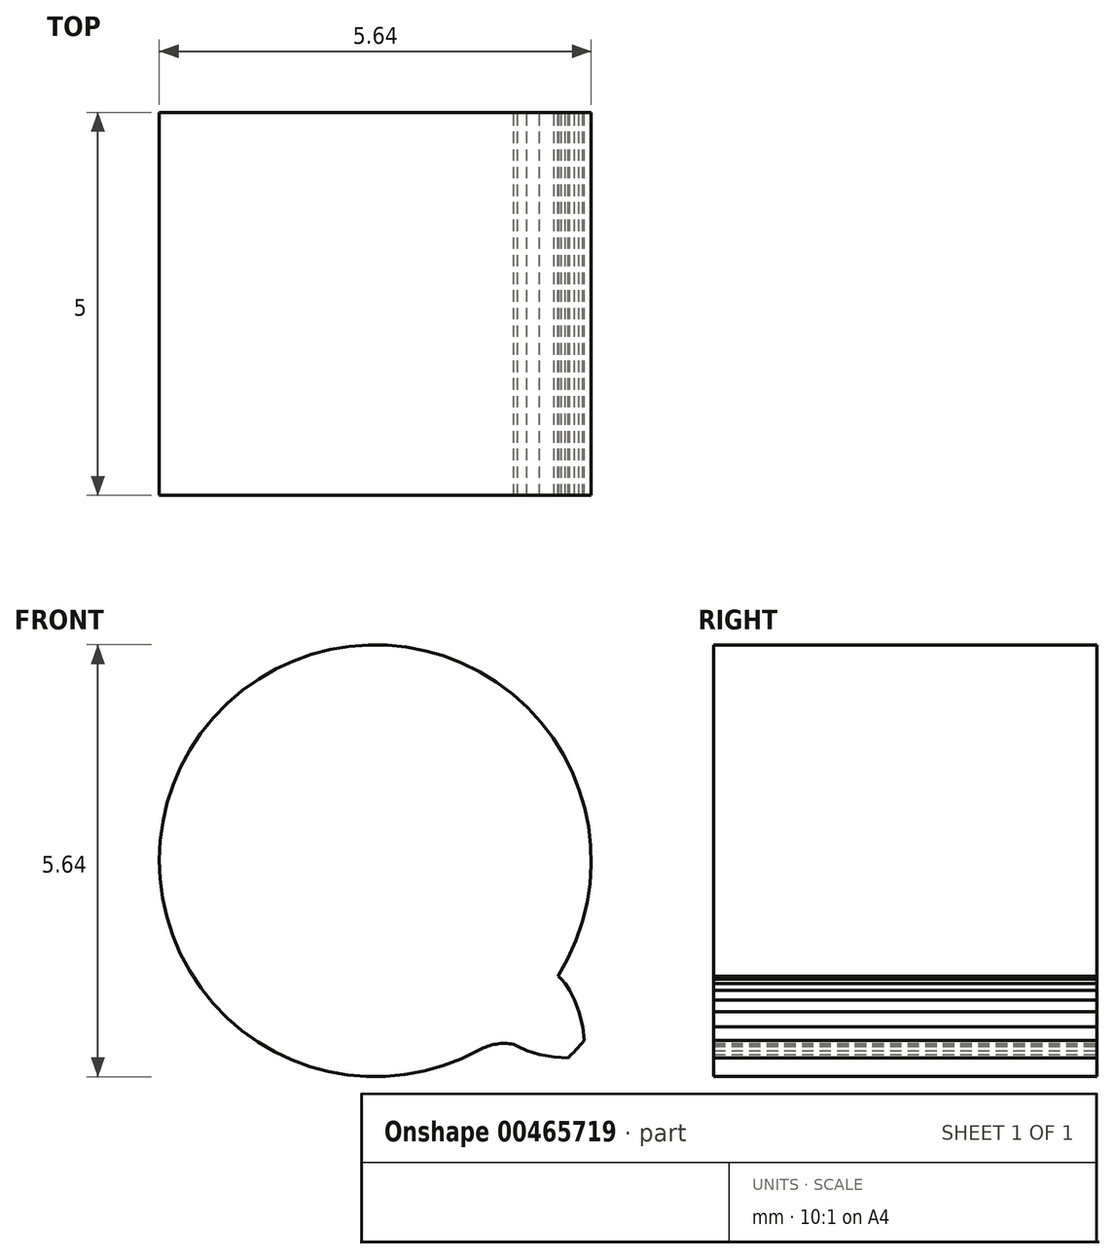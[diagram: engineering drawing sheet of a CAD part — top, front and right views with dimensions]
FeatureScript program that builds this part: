
annotation { "Feature Type Name" : "Feature", "Feature Type Description" : "" }
export const myFeature = defineFeature(function(context is Context, id is Id, definition is map)
    precondition{}
    {
        {
            var Q0;
            Q0=qCreatedBy(makeId("Front.planeOp"),FACE);
            var sketch = newSketch(context, id + "F0", { "sketchPlane" : qUnion([Q0])});
            skCircle(sketch, "E0", {"center": v(0, 0) * mm, "radius": 2.82 * mm});
            skCircle(sketch, "E1", {"center": v(0, 0) * mm, "radius": 3 * mm, "construction": true});
            skCircle(sketch, "E2", {"center": v(0, 0) * mm, "radius": 3.6 * mm, "construction": true});
            skLineSegment(sketch, "E3", {"start": v(0, 0) * mm, "end": v(0, 4.6) * mm, "construction": true});
            skLineSegment(sketch, "E4", {"start": v(0, 4.6) * mm, "end": v(0, 0) * mm, "construction": true});
            skLineSegment(sketch, "E5", {"start": v(0, 0) * mm, "end": v(-1.55, 4.33) * mm, "construction": true});
            skLineSegment(sketch, "E6", {"start": v(0, 2.82) * mm, "end": v(-2.7, 2.82) * mm, "construction": true});
            skLineSegment(sketch, "E7", {"start": v(0, 0) * mm, "end": v(-2.58, 3.55) * mm, "construction": true});
            skLineSegment(sketch, "E8", {"start": v(0, 0) * mm, "end": v(-1.24, 3.81) * mm, "construction": true});
            skLineSegment(sketch, "E9", {"start": v(0, 2.82) * mm, "end": v(2.06, 2.82) * mm, "construction": true});
            skLineSegment(sketch, "E10", {"start": v(0, 0) * mm, "end": v(-0.4, 3.74) * mm, "construction": true});
            skLineSegment(sketch, "E11", {"start": v(0, 0) * mm, "end": v(-0.82, 3.85) * mm, "construction": true});
            skLineSegment(sketch, "E12", {"start": v(0, 0) * mm, "end": v(-1.63, 3.66) * mm, "construction": true});
            skLineSegment(sketch, "E13", {"start": v(-0.3, 2.8) * mm, "end": v(0, 2.83) * mm, "construction": true});
            skLineSegment(sketch, "E14", {"start": v(-0.59, 2.76) * mm, "end": v(0, 2.88) * mm, "construction": true});
            skLineSegment(sketch, "E15", {"start": v(-0.87, 2.68) * mm, "end": v(-0.03, 2.95) * mm, "construction": true});
            skLineSegment(sketch, "E16", {"start": v(-1.15, 2.58) * mm, "end": v(-0.08, 3.05) * mm, "construction": true});
            skLineSegment(sketch, "E17", {"start": v(0, 0) * mm, "end": v(-1.97, 3.41) * mm, "construction": true});
            skLineSegment(sketch, "E18", {"start": v(-1.4, 2.44) * mm, "end": v(-0.15, 3.17) * mm, "construction": true});
            skLineSegment(sketch, "E19", {"start": v(-1.66, 2.28) * mm, "end": v(-0.25, 3.3) * mm, "construction": true});
            skLineSegment(sketch, "E20", {"start": v(0, 0) * mm, "end": v(-2.7, 3) * mm, "construction": true});
            skLineSegment(sketch, "E21", {"start": v(-1.89, 2.1) * mm, "end": v(-0.38, 3.45) * mm, "construction": true});
            skLineSegment(sketch, "E22", {"start": v(0, 2.82) * mm, "end": v(0, 2.83) * mm});
            skLineSegment(sketch, "E23", {"start": v(0, 2.88) * mm, "end": v(0, 2.83) * mm});
            skLineSegment(sketch, "E24", {"start": v(0, 2.88) * mm, "end": v(-0.03, 2.95) * mm});
            skLineSegment(sketch, "E25", {"start": v(-0.03, 2.95) * mm, "end": v(-0.08, 3.05) * mm});
            skLineSegment(sketch, "E26", {"start": v(-0.08, 3.05) * mm, "end": v(-0.15, 3.17) * mm});
            skLineSegment(sketch, "E27", {"start": v(-0.15, 3.17) * mm, "end": v(-0.25, 3.3) * mm});
            skLineSegment(sketch, "E28", {"start": v(-0.25, 3.3) * mm, "end": v(-0.38, 3.45) * mm});
            skLineSegment(sketch, "E29", {"start": v(0, 0) * mm, "end": v(-2.88, 2.6) * mm, "construction": true});
            skLineSegment(sketch, "E30", {"start": v(-2.1, 1.89) * mm, "end": v(-0.56, 3.6) * mm, "construction": true});
            skLineSegment(sketch, "E31", {"start": v(-0.56, 3.6) * mm, "end": v(-0.38, 3.45) * mm});
            skLineSegment(sketch, "E32", {"start": v(0, 0) * mm, "end": v(-0.81, 4.25) * mm});
            skLineSegment(sketch, "E33.MirrorCS", {"start": v(-0.8, 3.54) * mm, "end": v(-0.92, 3.34) * mm});
            skLineSegment(sketch, "E34.MirrorCS", {"start": v(-1, 3.16) * mm, "end": v(-0.92, 3.34) * mm});
            skLineSegment(sketch, "E35.MirrorCS", {"start": v(-1.04, 3) * mm, "end": v(-1, 3.16) * mm});
            skLineSegment(sketch, "E36.MirrorCS", {"start": v(-1.06, 2.86) * mm, "end": v(-1.04, 3) * mm});
            skLineSegment(sketch, "E37.MirrorCS", {"start": v(-1.06, 2.76) * mm, "end": v(-1.06, 2.86) * mm});
            skLineSegment(sketch, "E38.MirrorCS", {"start": v(-1.06, 2.68) * mm, "end": v(-1.06, 2.76) * mm});
            skLineSegment(sketch, "E39.MirrorCS", {"start": v(-1.06, 2.68) * mm, "end": v(-1.05, 2.63) * mm});
            skLineSegment(sketch, "E40.MirrorCS", {"start": v(-1.04, 2.62) * mm, "end": v(-1.05, 2.63) * mm});
            skArc(sketch, "E41", {"start": v(-0.52, 3.56) * mm, "mid": v(-0.68, 3.54) * mm, "end": v(-0.83, 3.5) * mm});
            skLineSegment(sketch, "E42", {"start": v(-0.05, 3) * mm, "end": v(0, 0) * mm, "construction": true});
            skLineSegment(sketch, "E43", {"start": v(0, 0) * mm, "end": v(-2.64, 3.5) * mm, "construction": true});
            skArc(sketch, "E44", {"start": v(-1.8, 2.4) * mm, "mid": v(-1.36, 2.47) * mm, "end": v(-1.06, 2.8) * mm});
            skLineSegment(sketch, "E45", {"start": v(0, 0) * mm, "end": v(-1.74, 5.05) * mm, "construction": true});
            skSolve(sketch);
        }
        {
            var Q0;
            Q0=qCreatedBy(makeId("Front.planeOp"),FACE);
            var sketch = newSketch(context, id + "F1", { "sketchPlane" : qUnion([Q0])});
            skCircle(sketch, "E46.0", {"center": v(0, 0) * mm, "radius": 2.82 * mm});
            skArc(sketch, "E47.0", {"start": v(-0.52, 3.56) * mm, "mid": v(-0.68, 3.54) * mm, "end": v(-0.83, 3.5) * mm});
            skLineSegment(sketch, "E47.1", {"start": v(-0.8, 3.54) * mm, "end": v(-0.92, 3.34) * mm});
            skLineSegment(sketch, "E47.2", {"start": v(-1, 3.16) * mm, "end": v(-0.92, 3.34) * mm});
            skLineSegment(sketch, "E47.3", {"start": v(-1.04, 3) * mm, "end": v(-1, 3.16) * mm});
            skLineSegment(sketch, "E47.4", {"start": v(-0.56, 3.6) * mm, "end": v(-0.38, 3.45) * mm});
            skLineSegment(sketch, "E47.5", {"start": v(-0.25, 3.3) * mm, "end": v(-0.38, 3.45) * mm});
            skLineSegment(sketch, "E47.6", {"start": v(-0.15, 3.17) * mm, "end": v(-0.25, 3.3) * mm});
            skLineSegment(sketch, "E47.7", {"start": v(-0.08, 3.05) * mm, "end": v(-0.15, 3.17) * mm});
            skLineSegment(sketch, "E47.8", {"start": v(-0.03, 2.95) * mm, "end": v(-0.08, 3.05) * mm});
            skLineSegment(sketch, "E47.9", {"start": v(0, 2.88) * mm, "end": v(-0.03, 2.95) * mm});
            skLineSegment(sketch, "E47.10", {"start": v(0, 2.88) * mm, "end": v(0, 2.83) * mm});
            skLineSegment(sketch, "E47.11", {"start": v(0, 2.82) * mm, "end": v(0, 2.83) * mm});
            skLineSegment(sketch, "E47.12", {"start": v(-1.06, 2.86) * mm, "end": v(-1.04, 3) * mm});
            skLineSegment(sketch, "E47.13", {"start": v(-1.06, 2.76) * mm, "end": v(-1.06, 2.86) * mm});
            skLineSegment(sketch, "E47.14", {"start": v(-1.06, 2.68) * mm, "end": v(-1.06, 2.76) * mm});
            skLineSegment(sketch, "E47.15", {"start": v(-1.06, 2.68) * mm, "end": v(-1.05, 2.63) * mm});
            skLineSegment(sketch, "E47.16", {"start": v(-1.04, 2.62) * mm, "end": v(-1.05, 2.63) * mm});
            skArc(sketch, "E48.0", {"start": v(-1.8, 2.4) * mm, "mid": v(-1.36, 2.47) * mm, "end": v(-1.06, 2.8) * mm});
            skArc(sketch, "E49.MirrorCS", {"start": v(0.8, 2.9) * mm, "mid": v(0.35, 2.8) * mm, "end": v(-0.05, 3) * mm});
            skArc(sketch, "E50.MirrorCS", {"start": v(-0.83, 3.5) * mm, "mid": v(-0.68, 3.54) * mm, "end": v(-0.52, 3.56) * mm});
            skLineSegment(sketch, "E51", {"start": v(-1.69, 3.06) * mm, "end": v(0, 0) * mm, "construction": true});
            skLineSegment(sketch, "E52.MirrorCS", {"start": v(-2.38, 1.5) * mm, "end": v(-2.4, 1.52) * mm});
            skLineSegment(sketch, "E53.MirrorCS", {"start": v(-2.43, 1.55) * mm, "end": v(-2.4, 1.52) * mm});
            skLineSegment(sketch, "E54.MirrorCS", {"start": v(-2.43, 1.55) * mm, "end": v(-2.48, 1.6) * mm});
            skLineSegment(sketch, "E55.MirrorCS", {"start": v(-2.48, 1.6) * mm, "end": v(-2.54, 1.7) * mm});
            skLineSegment(sketch, "E56.MirrorCS", {"start": v(-1.7, 2.32) * mm, "end": v(-1.67, 2.3) * mm});
            skLineSegment(sketch, "E57.MirrorCS", {"start": v(-1.7, 2.32) * mm, "end": v(-1.76, 2.37) * mm});
            skLineSegment(sketch, "E58.MirrorCS", {"start": v(-1.66, 2.28) * mm, "end": v(-1.67, 2.3) * mm});
            skLineSegment(sketch, "E59.MirrorCS", {"start": v(-1.76, 2.37) * mm, "end": v(-1.86, 2.42) * mm});
            skLineSegment(sketch, "E60.MirrorCS", {"start": v(-1.98, 2.48) * mm, "end": v(-2.14, 2.53) * mm});
            skLineSegment(sketch, "E61.MirrorCS", {"start": v(-1.86, 2.42) * mm, "end": v(-1.98, 2.48) * mm});
            skLineSegment(sketch, "E62.MirrorCS", {"start": v(-2.54, 1.7) * mm, "end": v(-2.6, 1.82) * mm});
            skLineSegment(sketch, "E63.MirrorCS", {"start": v(-2.6, 1.82) * mm, "end": v(-2.66, 1.97) * mm});
            skLineSegment(sketch, "E64.MirrorCS", {"start": v(-2.66, 1.97) * mm, "end": v(-2.7, 2.17) * mm});
            skLineSegment(sketch, "E65.MirrorCS", {"start": v(-2.56, 2.58) * mm, "end": v(-2.34, 2.56) * mm});
            skLineSegment(sketch, "E66.MirrorCS", {"start": v(-2.74, 2.4) * mm, "end": v(-2.7, 2.17) * mm});
            skArc(sketch, "E67.MirrorCS", {"start": v(-2.52, 2.57) * mm, "mid": v(-2.63, 2.46) * mm, "end": v(-2.73, 2.35) * mm});
            skLineSegment(sketch, "E68.MirrorCS", {"start": v(-2.14, 2.53) * mm, "end": v(-2.34, 2.56) * mm});
            skArc(sketch, "E69.MirrorCS", {"start": v(-1.06, 2.8) * mm, "mid": v(-1.36, 2.47) * mm, "end": v(-1.8, 2.4) * mm});
            skArc(sketch, "E70.MirrorCS", {"start": v(-2.73, 2.35) * mm, "mid": v(-2.63, 2.46) * mm, "end": v(-2.52, 2.57) * mm});
            skArc(sketch, "E71.MirrorCS", {"start": v(-2.87, 0.88) * mm, "mid": v(-2.55, 1.2) * mm, "end": v(-2.5, 1.65) * mm});
            skLineSegment(sketch, "E72", {"start": v(-3.16, 1.48) * mm, "end": v(0, 0) * mm, "construction": true});
            skLineSegment(sketch, "E73.MirrorCS", {"start": v(-2.17, -1.8) * mm, "end": v(-2.18, -1.81) * mm});
            skLineSegment(sketch, "E74.MirrorCS", {"start": v(-2.22, -1.83) * mm, "end": v(-2.18, -1.81) * mm});
            skLineSegment(sketch, "E75.MirrorCS", {"start": v(-2.74, -0.9) * mm, "end": v(-2.7, -0.88) * mm});
            skLineSegment(sketch, "E76.MirrorCS", {"start": v(-2.74, -0.9) * mm, "end": v(-2.8, -0.94) * mm});
            skLineSegment(sketch, "E77.MirrorCS", {"start": v(-2.22, -1.83) * mm, "end": v(-2.3, -1.86) * mm});
            skLineSegment(sketch, "E78.MirrorCS", {"start": v(-2.68, -0.87) * mm, "end": v(-2.7, -0.88) * mm});
            skLineSegment(sketch, "E79.MirrorCS", {"start": v(-2.8, -0.94) * mm, "end": v(-2.88, -1.02) * mm});
            skLineSegment(sketch, "E80.MirrorCS", {"start": v(-2.68, 0.87) * mm, "end": v(-2.7, 0.87) * mm});
            skLineSegment(sketch, "E81.MirrorCS", {"start": v(-2.3, -1.86) * mm, "end": v(-2.4, -1.9) * mm});
            skLineSegment(sketch, "E82.MirrorCS", {"start": v(-2.81, -0.18) * mm, "end": v(-2.83, -0.18) * mm});
            skLineSegment(sketch, "E83.MirrorCS", {"start": v(-2.53, -1.91) * mm, "end": v(-2.7, -1.92) * mm});
            skLineSegment(sketch, "E84.MirrorCS", {"start": v(-2.7, -1.92) * mm, "end": v(-2.9, -1.9) * mm});
            skLineSegment(sketch, "E85.MirrorCS", {"start": v(-2.87, -0.18) * mm, "end": v(-2.83, -0.18) * mm});
            skLineSegment(sketch, "E86.MirrorCS", {"start": v(-2.4, -1.9) * mm, "end": v(-2.53, -1.91) * mm});
            skLineSegment(sketch, "E87.MirrorCS", {"start": v(-2.74, 0.88) * mm, "end": v(-2.7, 0.87) * mm});
            skLineSegment(sketch, "E88.MirrorCS", {"start": v(-3.07, -1.26) * mm, "end": v(-3.16, -1.43) * mm});
            skLineSegment(sketch, "E89.MirrorCS", {"start": v(-2.88, -1.02) * mm, "end": v(-2.97, -1.12) * mm});
            skLineSegment(sketch, "E90.MirrorCS", {"start": v(-2.74, 0.88) * mm, "end": v(-2.82, 0.88) * mm});
            skLineSegment(sketch, "E91.MirrorCS", {"start": v(-2.97, -1.12) * mm, "end": v(-3.07, -1.26) * mm});
            skLineSegment(sketch, "E92.MirrorCS", {"start": v(-2.87, -0.18) * mm, "end": v(-2.95, -0.16) * mm});
            skLineSegment(sketch, "E93.MirrorCS", {"start": v(-2.95, -0.16) * mm, "end": v(-3.05, -0.12) * mm});
            skLineSegment(sketch, "E94.MirrorCS", {"start": v(-3.12, -1.86) * mm, "end": v(-2.9, -1.9) * mm});
            skLineSegment(sketch, "E95.MirrorCS", {"start": v(-3.17, -0.06) * mm, "end": v(-3.31, 0.03) * mm});
            skLineSegment(sketch, "E96.MirrorCS", {"start": v(-3.06, 0.84) * mm, "end": v(-3.22, 0.79) * mm});
            skLineSegment(sketch, "E97.MirrorCS", {"start": v(-2.82, 0.88) * mm, "end": v(-2.93, 0.87) * mm});
            skLineSegment(sketch, "E98.MirrorCS", {"start": v(-3.22, 0.79) * mm, "end": v(-3.4, 0.7) * mm});
            skLineSegment(sketch, "E99.MirrorCS", {"start": v(-3.31, 0.03) * mm, "end": v(-3.46, 0.16) * mm});
            skLineSegment(sketch, "E100.MirrorCS", {"start": v(-2.93, 0.87) * mm, "end": v(-3.06, 0.84) * mm});
            skLineSegment(sketch, "E101.MirrorCS", {"start": v(-3.05, -0.12) * mm, "end": v(-3.17, -0.06) * mm});
            skLineSegment(sketch, "E102.MirrorCS", {"start": v(-3.24, -1.64) * mm, "end": v(-3.16, -1.43) * mm});
            skLineSegment(sketch, "E103.MirrorCS", {"start": v(-3.59, 0.58) * mm, "end": v(-3.4, 0.7) * mm});
            skLineSegment(sketch, "E104.MirrorCS", {"start": v(-3.62, 0.33) * mm, "end": v(-3.46, 0.16) * mm});
            skArc(sketch, "E105.MirrorCS", {"start": v(-3.59, 0.3) * mm, "mid": v(-3.57, 0.45) * mm, "end": v(-3.55, 0.6) * mm});
            skArc(sketch, "E106.MirrorCS", {"start": v(-3.22, -1.6) * mm, "mid": v(-3.15, -1.74) * mm, "end": v(-3.08, -1.87) * mm});
            skArc(sketch, "E107.MirrorCS", {"start": v(-3.55, 0.6) * mm, "mid": v(-3.57, 0.45) * mm, "end": v(-3.59, 0.3) * mm});
            skArc(sketch, "E108.MirrorCS", {"start": v(-3.08, -1.87) * mm, "mid": v(-3.15, -1.74) * mm, "end": v(-3.22, -1.6) * mm});
            skArc(sketch, "E109.MirrorCS", {"start": v(-3, -0.14) * mm, "mid": v(-2.77, -0.53) * mm, "end": v(-2.84, -0.98) * mm});
            skArc(sketch, "E110.MirrorCS", {"start": v(-2.5, 1.65) * mm, "mid": v(-2.55, 1.2) * mm, "end": v(-2.87, 0.88) * mm});
            skArc(sketch, "E111.MirrorCS", {"start": v(-2.84, -0.98) * mm, "mid": v(-2.77, -0.53) * mm, "end": v(-3, -0.14) * mm});
            skArc(sketch, "E112.MirrorCS", {"start": v(-1.72, -2.46) * mm, "mid": v(-1.93, -2.06) * mm, "end": v(-2.34, -1.88) * mm});
            skLineSegment(sketch, "E113", {"start": v(0, 0) * mm, "end": v(-2.39, -2.55) * mm, "construction": true});
            skLineSegment(sketch, "E114.MirrorCS", {"start": v(2.81, 0.18) * mm, "end": v(2.83, 0.18) * mm});
            skLineSegment(sketch, "E115.MirrorCS", {"start": v(2.87, 0.18) * mm, "end": v(2.83, 0.18) * mm});
            skLineSegment(sketch, "E116.MirrorCS", {"start": v(-1.66, -2.28) * mm, "end": v(-1.67, -2.3) * mm});
            skLineSegment(sketch, "E117.MirrorCS", {"start": v(-0.7, -2.73) * mm, "end": v(-0.7, -2.75) * mm});
            skLineSegment(sketch, "E118.MirrorCS", {"start": v(1.66, -2.28) * mm, "end": v(1.67, -2.3) * mm});
            skLineSegment(sketch, "E119.MirrorCS", {"start": v(-1.69, -2.34) * mm, "end": v(-1.7, -2.4) * mm});
            skLineSegment(sketch, "E120.MirrorCS", {"start": v(1.04, -2.62) * mm, "end": v(1.05, -2.63) * mm});
            skLineSegment(sketch, "E121.MirrorCS", {"start": v(-1.69, -2.34) * mm, "end": v(-1.67, -2.3) * mm});
            skLineSegment(sketch, "E122.MirrorCS", {"start": v(2.74, -0.88) * mm, "end": v(2.7, -0.87) * mm});
            skLineSegment(sketch, "E123.MirrorCS", {"start": v(2.74, -0.88) * mm, "end": v(2.82, -0.88) * mm});
            skLineSegment(sketch, "E124.MirrorCS", {"start": v(2.87, 0.18) * mm, "end": v(2.95, 0.16) * mm});
            skLineSegment(sketch, "E125.MirrorCS", {"start": v(2.68, -0.87) * mm, "end": v(2.7, -0.87) * mm});
            skLineSegment(sketch, "E126.MirrorCS", {"start": v(2.43, -1.55) * mm, "end": v(2.48, -1.6) * mm});
            skLineSegment(sketch, "E127.MirrorCS", {"start": v(-0.76, -2.85) * mm, "end": v(-0.83, -2.94) * mm});
            skLineSegment(sketch, "E128.MirrorCS", {"start": v(1.7, -2.32) * mm, "end": v(1.67, -2.3) * mm});
            skLineSegment(sketch, "E129.MirrorCS", {"start": v(-0.72, -2.79) * mm, "end": v(-0.7, -2.75) * mm});
            skLineSegment(sketch, "E130.MirrorCS", {"start": v(1.06, -2.68) * mm, "end": v(1.05, -2.63) * mm});
            skLineSegment(sketch, "E131.MirrorCS", {"start": v(-0.72, -2.79) * mm, "end": v(-0.76, -2.85) * mm});
            skLineSegment(sketch, "E132.MirrorCS", {"start": v(2.95, 0.16) * mm, "end": v(3.05, 0.12) * mm});
            skLineSegment(sketch, "E133.MirrorCS", {"start": v(1.7, -2.32) * mm, "end": v(1.76, -2.37) * mm});
            skLineSegment(sketch, "E134.MirrorCS", {"start": v(1.06, -2.68) * mm, "end": v(1.06, -2.76) * mm});
            skLineSegment(sketch, "E135.MirrorCS", {"start": v(1.76, -2.37) * mm, "end": v(1.86, -2.42) * mm});
            skLineSegment(sketch, "E136.MirrorCS", {"start": v(-1.7, -2.4) * mm, "end": v(-1.73, -2.51) * mm});
            skLineSegment(sketch, "E137.MirrorCS", {"start": v(2.48, -1.6) * mm, "end": v(2.54, -1.7) * mm});
            skLineSegment(sketch, "E138.MirrorCS", {"start": v(2.82, -0.88) * mm, "end": v(2.93, -0.87) * mm});
            skLineSegment(sketch, "E139.MirrorCS", {"start": v(1.06, -2.76) * mm, "end": v(1.06, -2.86) * mm});
            skLineSegment(sketch, "E140.MirrorCS", {"start": v(3.17, 0.06) * mm, "end": v(3.31, -0.03) * mm});
            skLineSegment(sketch, "E141.MirrorCS", {"start": v(2.93, -0.87) * mm, "end": v(3.06, -0.84) * mm});
            skLineSegment(sketch, "E142.MirrorCS", {"start": v(3.05, 0.12) * mm, "end": v(3.17, 0.06) * mm});
            skLineSegment(sketch, "E143.MirrorCS", {"start": v(2.43, -1.55) * mm, "end": v(2.4, -1.52) * mm});
            skLineSegment(sketch, "E144.MirrorCS", {"start": v(3.31, -0.03) * mm, "end": v(3.46, -0.16) * mm});
            skLineSegment(sketch, "E145.MirrorCS", {"start": v(0.03, -2.95) * mm, "end": v(0.08, -3.05) * mm});
            skLineSegment(sketch, "E146.MirrorCS", {"start": v(0, -2.88) * mm, "end": v(0, -2.83) * mm});
            skLineSegment(sketch, "E147.MirrorCS", {"start": v(1.86, -2.42) * mm, "end": v(1.98, -2.48) * mm});
            skLineSegment(sketch, "E148.MirrorCS", {"start": v(3.22, -0.79) * mm, "end": v(3.4, -0.7) * mm});
            skLineSegment(sketch, "E149.MirrorCS", {"start": v(2.38, -1.5) * mm, "end": v(2.4, -1.52) * mm});
            skLineSegment(sketch, "E150.MirrorCS", {"start": v(0, -2.82) * mm, "end": v(0, -2.83) * mm});
            skLineSegment(sketch, "E151.MirrorCS", {"start": v(3.06, -0.84) * mm, "end": v(3.22, -0.79) * mm});
            skLineSegment(sketch, "E152.MirrorCS", {"start": v(0, -2.88) * mm, "end": v(0.03, -2.95) * mm});
            skLineSegment(sketch, "E153.MirrorCS", {"start": v(-1.75, -2.65) * mm, "end": v(-1.74, -2.82) * mm});
            skLineSegment(sketch, "E154.MirrorCS", {"start": v(2.54, -1.7) * mm, "end": v(2.6, -1.82) * mm});
            skLineSegment(sketch, "E155.MirrorCS", {"start": v(-1.73, -2.51) * mm, "end": v(-1.75, -2.65) * mm});
            skLineSegment(sketch, "E156.MirrorCS", {"start": v(1.06, -2.86) * mm, "end": v(1.04, -3) * mm});
            skArc(sketch, "E157.MirrorCS", {"start": v(2.73, -2.35) * mm, "mid": v(2.63, -2.46) * mm, "end": v(2.52, -2.57) * mm});
            skLineSegment(sketch, "E158.MirrorCS", {"start": v(0.15, -3.17) * mm, "end": v(0.25, -3.3) * mm});
            skLineSegment(sketch, "E159.MirrorCS", {"start": v(2.66, -1.97) * mm, "end": v(2.7, -2.17) * mm});
            skLineSegment(sketch, "E160.MirrorCS", {"start": v(2.6, -1.82) * mm, "end": v(2.66, -1.97) * mm});
            skLineSegment(sketch, "E161.MirrorCS", {"start": v(-1.74, -2.82) * mm, "end": v(-1.71, -3.01) * mm});
            skLineSegment(sketch, "E162.MirrorCS", {"start": v(0.8, -3.54) * mm, "end": v(0.92, -3.34) * mm});
            skLineSegment(sketch, "E163.MirrorCS", {"start": v(1.04, -3) * mm, "end": v(1, -3.16) * mm});
            skLineSegment(sketch, "E164.MirrorCS", {"start": v(-1.06, -3.14) * mm, "end": v(-1.22, -3.25) * mm});
            skLineSegment(sketch, "E165.MirrorCS", {"start": v(1.98, -2.48) * mm, "end": v(2.14, -2.53) * mm});
            skLineSegment(sketch, "E166.MirrorCS", {"start": v(1, -3.16) * mm, "end": v(0.92, -3.34) * mm});
            skLineSegment(sketch, "E167.MirrorCS", {"start": v(-0.83, -2.94) * mm, "end": v(-0.92, -3.04) * mm});
            skLineSegment(sketch, "E168.MirrorCS", {"start": v(2.56, -2.58) * mm, "end": v(2.34, -2.56) * mm});
            skLineSegment(sketch, "E169.MirrorCS", {"start": v(2.14, -2.53) * mm, "end": v(2.34, -2.56) * mm});
            skLineSegment(sketch, "E170.MirrorCS", {"start": v(0.25, -3.3) * mm, "end": v(0.38, -3.45) * mm});
            skLineSegment(sketch, "E171.MirrorCS", {"start": v(-0.92, -3.04) * mm, "end": v(-1.06, -3.14) * mm});
            skLineSegment(sketch, "E172.MirrorCS", {"start": v(3.62, -0.33) * mm, "end": v(3.46, -0.16) * mm});
            skLineSegment(sketch, "E173.MirrorCS", {"start": v(2.74, -2.4) * mm, "end": v(2.7, -2.17) * mm});
            skLineSegment(sketch, "E174.MirrorCS", {"start": v(0.08, -3.05) * mm, "end": v(0.15, -3.17) * mm});
            skArc(sketch, "E175.MirrorCS", {"start": v(3.55, -0.6) * mm, "mid": v(3.57, -0.45) * mm, "end": v(3.59, -0.3) * mm});
            skArc(sketch, "E176.MirrorCS", {"start": v(2.52, -2.57) * mm, "mid": v(2.63, -2.46) * mm, "end": v(2.73, -2.35) * mm});
            skLineSegment(sketch, "E177.MirrorCS", {"start": v(0.56, -3.6) * mm, "end": v(0.38, -3.45) * mm});
            skLineSegment(sketch, "E178.MirrorCS", {"start": v(3.59, -0.58) * mm, "end": v(3.4, -0.7) * mm});
            skLineSegment(sketch, "E179.MirrorCS", {"start": v(-1.66, -3.23) * mm, "end": v(-1.71, -3.01) * mm});
            skLineSegment(sketch, "E180.MirrorCS", {"start": v(-1.43, -3.34) * mm, "end": v(-1.22, -3.25) * mm});
            skArc(sketch, "E181.MirrorCS", {"start": v(0.52, -3.56) * mm, "mid": v(0.68, -3.54) * mm, "end": v(0.83, -3.5) * mm});
            skArc(sketch, "E182.MirrorCS", {"start": v(-1.39, -3.32) * mm, "mid": v(-1.53, -3.26) * mm, "end": v(-1.67, -3.19) * mm});
            skArc(sketch, "E183.MirrorCS", {"start": v(3.59, -0.3) * mm, "mid": v(3.57, -0.45) * mm, "end": v(3.55, -0.6) * mm});
            skArc(sketch, "E184.MirrorCS", {"start": v(0.83, -3.5) * mm, "mid": v(0.68, -3.54) * mm, "end": v(0.52, -3.56) * mm});
            skArc(sketch, "E185.MirrorCS", {"start": v(-1.67, -3.19) * mm, "mid": v(-1.53, -3.26) * mm, "end": v(-1.39, -3.32) * mm});
            skArc(sketch, "E186.MirrorCS", {"start": v(2.87, -0.88) * mm, "mid": v(2.55, -1.2) * mm, "end": v(2.5, -1.65) * mm});
            skArc(sketch, "E187.MirrorCS", {"start": v(0.05, -3) * mm, "mid": v(-0.35, -2.8) * mm, "end": v(-0.8, -2.9) * mm});
            skArc(sketch, "E188.MirrorCS", {"start": v(2.5, -1.65) * mm, "mid": v(2.55, -1.2) * mm, "end": v(2.87, -0.88) * mm});
            skLineSegment(sketch, "E189.MirrorCS", {"start": v(3.16, -1.48) * mm, "end": v(0, 0) * mm, "construction": true});
            skArc(sketch, "E190.MirrorCS", {"start": v(1.06, -2.8) * mm, "mid": v(1.36, -2.47) * mm, "end": v(1.8, -2.4) * mm});
            skArc(sketch, "E191.MirrorCS", {"start": v(-2.34, -1.88) * mm, "mid": v(-1.93, -2.06) * mm, "end": v(-1.72, -2.46) * mm});
            skArc(sketch, "E192.MirrorCS", {"start": v(2.84, 0.98) * mm, "mid": v(2.77, 0.53) * mm, "end": v(3, 0.14) * mm});
            skLineSegment(sketch, "E193.MirrorCS", {"start": v(1.69, -3.06) * mm, "end": v(0, 0) * mm, "construction": true});
            skArc(sketch, "E194.MirrorCS", {"start": v(-0.8, -2.9) * mm, "mid": v(-0.35, -2.8) * mm, "end": v(0.05, -3) * mm});
            skArc(sketch, "E195.MirrorCS", {"start": v(1.8, -2.4) * mm, "mid": v(1.36, -2.47) * mm, "end": v(1.06, -2.8) * mm});
            skLineSegment(sketch, "E196.MirrorCS", {"start": v(2.68, 0.87) * mm, "end": v(2.7, 0.88) * mm});
            skLineSegment(sketch, "E197.MirrorCS", {"start": v(2.74, 0.9) * mm, "end": v(2.7, 0.88) * mm});
            skLineSegment(sketch, "E198.MirrorCS", {"start": v(2.17, 1.8) * mm, "end": v(2.18, 1.81) * mm});
            skLineSegment(sketch, "E199.MirrorCS", {"start": v(2.74, 0.9) * mm, "end": v(2.8, 0.94) * mm});
            skLineSegment(sketch, "E200.MirrorCS", {"start": v(0.7, 2.73) * mm, "end": v(0.7, 2.75) * mm});
            skLineSegment(sketch, "E201.MirrorCS", {"start": v(2.22, 1.83) * mm, "end": v(2.3, 1.86) * mm});
            skLineSegment(sketch, "E202.MirrorCS", {"start": v(2.22, 1.83) * mm, "end": v(2.18, 1.81) * mm});
            skLineSegment(sketch, "E203.MirrorCS", {"start": v(0.72, 2.79) * mm, "end": v(0.7, 2.75) * mm});
            skLineSegment(sketch, "E204.MirrorCS", {"start": v(0.72, 2.79) * mm, "end": v(0.76, 2.85) * mm});
            skLineSegment(sketch, "E205.MirrorCS", {"start": v(2.3, 1.86) * mm, "end": v(2.4, 1.9) * mm});
            skLineSegment(sketch, "E206.MirrorCS", {"start": v(2.8, 0.94) * mm, "end": v(2.88, 1.02) * mm});
            skLineSegment(sketch, "E207.MirrorCS", {"start": v(0.76, 2.85) * mm, "end": v(0.83, 2.94) * mm});
            skLineSegment(sketch, "E208.MirrorCS", {"start": v(1.69, 2.34) * mm, "end": v(1.7, 2.4) * mm});
            skLineSegment(sketch, "E209.MirrorCS", {"start": v(1.73, 2.51) * mm, "end": v(1.75, 2.65) * mm});
            skLineSegment(sketch, "E210.MirrorCS", {"start": v(1.66, 2.28) * mm, "end": v(1.67, 2.3) * mm});
            skLineSegment(sketch, "E211.MirrorCS", {"start": v(1.7, 2.4) * mm, "end": v(1.73, 2.51) * mm});
            skLineSegment(sketch, "E212.MirrorCS", {"start": v(1.69, 2.34) * mm, "end": v(1.67, 2.3) * mm});
            skLineSegment(sketch, "E213.MirrorCS", {"start": v(2.88, 1.02) * mm, "end": v(2.97, 1.12) * mm});
            skLineSegment(sketch, "E214.MirrorCS", {"start": v(0.83, 2.94) * mm, "end": v(0.92, 3.04) * mm});
            skLineSegment(sketch, "E215.MirrorCS", {"start": v(2.97, 1.12) * mm, "end": v(3.07, 1.26) * mm});
            skLineSegment(sketch, "E216.MirrorCS", {"start": v(2.53, 1.91) * mm, "end": v(2.7, 1.92) * mm});
            skLineSegment(sketch, "E217.MirrorCS", {"start": v(1.74, 2.82) * mm, "end": v(1.71, 3.01) * mm});
            skLineSegment(sketch, "E218.MirrorCS", {"start": v(1.43, 3.34) * mm, "end": v(1.22, 3.25) * mm});
            skLineSegment(sketch, "E219.MirrorCS", {"start": v(1.75, 2.65) * mm, "end": v(1.74, 2.82) * mm});
            skLineSegment(sketch, "E220.MirrorCS", {"start": v(2.4, 1.9) * mm, "end": v(2.53, 1.91) * mm});
            skLineSegment(sketch, "E221.MirrorCS", {"start": v(1.06, 3.14) * mm, "end": v(1.22, 3.25) * mm});
            skArc(sketch, "E222.MirrorCS", {"start": v(1.67, 3.19) * mm, "mid": v(1.53, 3.26) * mm, "end": v(1.39, 3.32) * mm});
            skLineSegment(sketch, "E223.MirrorCS", {"start": v(3.07, 1.26) * mm, "end": v(3.16, 1.43) * mm});
            skLineSegment(sketch, "E224.MirrorCS", {"start": v(2.7, 1.92) * mm, "end": v(2.9, 1.9) * mm});
            skLineSegment(sketch, "E225.MirrorCS", {"start": v(0.92, 3.04) * mm, "end": v(1.06, 3.14) * mm});
            skLineSegment(sketch, "E226.MirrorCS", {"start": v(1.66, 3.23) * mm, "end": v(1.71, 3.01) * mm});
            skArc(sketch, "E227.MirrorCS", {"start": v(1.39, 3.32) * mm, "mid": v(1.53, 3.26) * mm, "end": v(1.67, 3.19) * mm});
            skArc(sketch, "E228.MirrorCS", {"start": v(3.08, 1.87) * mm, "mid": v(3.15, 1.74) * mm, "end": v(3.22, 1.6) * mm});
            skLineSegment(sketch, "E229.MirrorCS", {"start": v(3.24, 1.64) * mm, "end": v(3.16, 1.43) * mm});
            skLineSegment(sketch, "E230.MirrorCS", {"start": v(3.12, 1.86) * mm, "end": v(2.9, 1.9) * mm});
            skArc(sketch, "E231.MirrorCS", {"start": v(3.22, 1.6) * mm, "mid": v(3.15, 1.74) * mm, "end": v(3.08, 1.87) * mm});
            skArc(sketch, "E232.MirrorCS", {"start": v(1.72, 2.46) * mm, "mid": v(1.93, 2.06) * mm, "end": v(2.34, 1.88) * mm});
            skLineSegment(sketch, "E233.MirrorCS", {"start": v(0, 0) * mm, "end": v(3.43, 0.66) * mm, "construction": true});
            skArc(sketch, "E234.MirrorCS", {"start": v(3, 0.14) * mm, "mid": v(2.77, 0.53) * mm, "end": v(2.84, 0.98) * mm});
            skArc(sketch, "E235.MirrorCS", {"start": v(2.34, 1.88) * mm, "mid": v(1.93, 2.06) * mm, "end": v(1.72, 2.46) * mm});
            skArc(sketch, "E236.MirrorCS", {"start": v(-0.05, 3) * mm, "mid": v(0.35, 2.8) * mm, "end": v(0.8, 2.9) * mm});
            skLineSegment(sketch, "E237.MirrorCS", {"start": v(-0.43, -3.47) * mm, "end": v(0, 0) * mm, "construction": true});
            skLineSegment(sketch, "E238.MirrorCS", {"start": v(0.43, 3.47) * mm, "end": v(0, 0) * mm, "construction": true});
            skSolve(sketch);
        }
        {
            var Q0;
            {var subQ0=sQuery(id+"F0.wireOp",EDGE,"E0");var subQ1=makeQuery(id+"F0.imprint","INTERSECT",VERTEX,{"derivedFrom":[subQ0,sQuery(id+"F0.wireOp",EDGE,"E22")]});Q0=makeQuery(id+"F0.imprint","IMPRINT",FACE,{"disambiguationData":[TD([[makeQuery(id+"F0.imprint","IMPRINT",EDGE,{"disambiguationData":[TD([[subQ1,-1.0]])],"derivedFrom":subQ0}),1.0]])]});}
            extrude(context, id + "F2", {"entities" : qUnion([Q0]), "depth" : 5 * mm});
        }
        {
            var Q0;
            {var subQ1=sQuery(id+"F1.wireOp",EDGE,"E199.MirrorCS");Q0=makeQuery(id+"F1.imprint","IMPRINT",FACE,{"disambiguationData":[TD([[makeQuery(id+"F1.imprint","IMPRINT",EDGE,{"derivedFrom":subQ1}),1.0]])]});}
            var Q1;
            {var subQ4=sQuery(id+"F1.wireOp",EDGE,"E114.MirrorCS");Q1=makeQuery(id+"F1.imprint","IMPRINT",FACE,{"disambiguationData":[TD([[makeQuery(id+"F1.imprint","IMPRINT",EDGE,{"derivedFrom":subQ4}),-1.0]])]});}
            var Q2;
            Q2=makeQuery(id+"F1.imprint","IMPRINT",FACE,{"disambiguationData":[TD([[makeQuery(id+"F1.imprint","IMPRINT",EDGE,{"derivedFrom":sQuery(id+"F1.wireOp",EDGE,"E128.MirrorCS")}),-1.0]])]});
            var Q3;
            {var subQ11=sQuery(id+"F1.wireOp",EDGE,"E120.MirrorCS");Q3=makeQuery(id+"F1.imprint","IMPRINT",FACE,{"disambiguationData":[TD([[makeQuery(id+"F1.imprint","IMPRINT",EDGE,{"derivedFrom":subQ11}),-1.0]])]});}
            var Q4;
            {var subQ8=sQuery(id+"F1.wireOp",EDGE,"E52.MirrorCS");Q4=makeQuery(id+"F1.imprint","IMPRINT",FACE,{"disambiguationData":[TD([[makeQuery(id+"F1.imprint","IMPRINT",EDGE,{"derivedFrom":subQ8}),-1.0]])]});}
            var Q5;
            {var subQ13=sQuery(id+"F1.wireOp",EDGE,"E200.MirrorCS");Q5=makeQuery(id+"F1.imprint","IMPRINT",FACE,{"disambiguationData":[TD([[makeQuery(id+"F1.imprint","IMPRINT",EDGE,{"derivedFrom":subQ13}),-1.0]])]});}
            var Q6;
            {var subQ6=sQuery(id+"F1.wireOp",EDGE,"E47.11");Q6=makeQuery(id+"F1.imprint","IMPRINT",FACE,{"disambiguationData":[TD([[makeQuery(id+"F1.imprint","IMPRINT",EDGE,{"derivedFrom":subQ6}),1.0]])]});}
            var Q7;
            {var subQ6=sQuery(id+"F1.wireOp",EDGE,"E80.MirrorCS");Q7=makeQuery(id+"F1.imprint","IMPRINT",FACE,{"disambiguationData":[TD([[makeQuery(id+"F1.imprint","IMPRINT",EDGE,{"derivedFrom":subQ6}),1.0]])]});}
            var Q8;
            Q8=makeQuery(id+"F1.imprint","IMPRINT",FACE,{"disambiguationData":[TD([[makeQuery(id+"F1.imprint","IMPRINT",EDGE,{"derivedFrom":sQuery(id+"F1.wireOp",EDGE,"E74.MirrorCS")}),1.0]])]});
            var Q9;
            Q9=makeQuery(id+"F1.imprint","IMPRINT",FACE,{"disambiguationData":[TD([[makeQuery(id+"F1.imprint","IMPRINT",EDGE,{"derivedFrom":sQuery(id+"F1.wireOp",EDGE,"E153.MirrorCS")}),1.0]])]});
            var Q10;
            {var subQ1=sQuery(id+"F1.wireOp",EDGE,"E47.14");Q10=makeQuery(id+"F1.imprint","IMPRINT",FACE,{"disambiguationData":[TD([[makeQuery(id+"F1.imprint","IMPRINT",EDGE,{"derivedFrom":subQ1}),1.0]])]});}
            var Q11;
            {var subQ0=sQuery(id+"F1.wireOp",EDGE,"E57.MirrorCS");Q11=makeQuery(id+"F1.imprint","IMPRINT",FACE,{"disambiguationData":[TD([[makeQuery(id+"F1.imprint","IMPRINT",EDGE,{"derivedFrom":subQ0}),-1.0]])]});}
            var Q12;
            {var subQ0=sQuery(id+"F1.wireOp",EDGE,"E52.MirrorCS");Q12=makeQuery(id+"F1.imprint","IMPRINT",FACE,{"disambiguationData":[TD([[makeQuery(id+"F1.imprint","IMPRINT",EDGE,{"derivedFrom":subQ0}),1.0]])]});}
            var Q13;
            {var subQ1=sQuery(id+"F1.wireOp",EDGE,"E80.MirrorCS");Q13=makeQuery(id+"F1.imprint","IMPRINT",FACE,{"disambiguationData":[TD([[makeQuery(id+"F1.imprint","IMPRINT",EDGE,{"derivedFrom":subQ1}),-1.0]])]});}
            var Q14;
            {var subQ1=sQuery(id+"F1.wireOp",EDGE,"E82.MirrorCS");Q14=makeQuery(id+"F1.imprint","IMPRINT",FACE,{"disambiguationData":[TD([[makeQuery(id+"F1.imprint","IMPRINT",EDGE,{"derivedFrom":subQ1}),1.0]])]});}
            var Q15;
            Q15=makeQuery(id+"F1.imprint","IMPRINT",FACE,{"disambiguationData":[TD([[makeQuery(id+"F1.imprint","IMPRINT",EDGE,{"derivedFrom":sQuery(id+"F1.wireOp",EDGE,"E75.MirrorCS")}),1.0]])]});
            var Q16;
            Q16=makeQuery(id+"F1.imprint","IMPRINT",FACE,{"disambiguationData":[TD([[makeQuery(id+"F1.imprint","IMPRINT",EDGE,{"derivedFrom":sQuery(id+"F1.wireOp",EDGE,"E74.MirrorCS")}),-1.0]])]});
            var Q17;
            Q17=makeQuery(id+"F1.imprint","IMPRINT",FACE,{"disambiguationData":[TD([[makeQuery(id+"F1.imprint","IMPRINT",EDGE,{"derivedFrom":sQuery(id+"F1.wireOp",EDGE,"E121.MirrorCS")}),1.0]])]});
            var Q18;
            {var subQ4=sQuery(id+"F1.wireOp",EDGE,"E199.MirrorCS");Q18=makeQuery(id+"F1.imprint","IMPRINT",FACE,{"disambiguationData":[TD([[makeQuery(id+"F1.imprint","IMPRINT",EDGE,{"derivedFrom":subQ4}),-1.0]])]});}
            var Q19;
            {var subQ0=sQuery(id+"F1.wireOp",EDGE,"E114.MirrorCS");Q19=makeQuery(id+"F1.imprint","IMPRINT",FACE,{"disambiguationData":[TD([[makeQuery(id+"F1.imprint","IMPRINT",EDGE,{"derivedFrom":subQ0}),1.0]])]});}
            var Q20;
            {var subQ6=sQuery(id+"F1.wireOp",EDGE,"E198.MirrorCS");Q20=makeQuery(id+"F1.imprint","IMPRINT",FACE,{"disambiguationData":[TD([[makeQuery(id+"F1.imprint","IMPRINT",EDGE,{"derivedFrom":subQ6}),1.0]])]});}
            var Q21;
            {var subQ1=sQuery(id+"F1.wireOp",EDGE,"E208.MirrorCS");Q21=makeQuery(id+"F1.imprint","IMPRINT",FACE,{"disambiguationData":[TD([[makeQuery(id+"F1.imprint","IMPRINT",EDGE,{"derivedFrom":subQ1}),-1.0]])]});}
            var Q22;
            {var subQ1=sQuery(id+"F1.wireOp",EDGE,"E200.MirrorCS");Q22=makeQuery(id+"F1.imprint","IMPRINT",FACE,{"disambiguationData":[TD([[makeQuery(id+"F1.imprint","IMPRINT",EDGE,{"derivedFrom":subQ1}),1.0]])]});}
            var Q23;
            {var subQ4=sQuery(id+"F1.wireOp",EDGE,"E47.11");Q23=makeQuery(id+"F1.imprint","IMPRINT",FACE,{"disambiguationData":[TD([[makeQuery(id+"F1.imprint","IMPRINT",EDGE,{"derivedFrom":subQ4}),-1.0]])]});}
            var Q24;
            Q24=makeQuery(id+"F1.imprint","IMPRINT",FACE,{"disambiguationData":[TD([[makeQuery(id+"F1.imprint","IMPRINT",EDGE,{"derivedFrom":sQuery(id+"F1.wireOp",EDGE,"E143.MirrorCS")}),-1.0]])]});
            var Q25;
            {var subQ1=sQuery(id+"F1.wireOp",EDGE,"E125.MirrorCS");Q25=makeQuery(id+"F1.imprint","IMPRINT",FACE,{"disambiguationData":[TD([[makeQuery(id+"F1.imprint","IMPRINT",EDGE,{"derivedFrom":subQ1}),-1.0]])]});}
            var Q26;
            Q26=makeQuery(id+"F1.imprint","IMPRINT",FACE,{"disambiguationData":[TD([[makeQuery(id+"F1.imprint","IMPRINT",EDGE,{"derivedFrom":sQuery(id+"F1.wireOp",EDGE,"E128.MirrorCS")}),1.0]])]});
            var Q27;
            {var subQ1=sQuery(id+"F1.wireOp",EDGE,"E120.MirrorCS");Q27=makeQuery(id+"F1.imprint","IMPRINT",FACE,{"disambiguationData":[TD([[makeQuery(id+"F1.imprint","IMPRINT",EDGE,{"derivedFrom":subQ1}),1.0]])]});}
            var Q28;
            {var subQ4=sQuery(id+"F1.wireOp",EDGE,"E150.MirrorCS");Q28=makeQuery(id+"F1.imprint","IMPRINT",FACE,{"disambiguationData":[TD([[makeQuery(id+"F1.imprint","IMPRINT",EDGE,{"derivedFrom":subQ4}),-1.0]])]});}
            var Q29;
            {var subQ1=sQuery(id+"F1.wireOp",EDGE,"E117.MirrorCS");Q29=makeQuery(id+"F1.imprint","IMPRINT",FACE,{"disambiguationData":[TD([[makeQuery(id+"F1.imprint","IMPRINT",EDGE,{"derivedFrom":subQ1}),1.0]])]});}
            extrude(context, id + "F3", {"entities" : qUnion([Q0, Q1, Q2, Q3, Q4, Q5, Q6, Q7, Q8, Q9, Q10, Q11, Q12, Q13, Q14, Q15, Q16, Q17, Q18, Q19, Q20, Q21, Q22, Q23, Q24, Q25, Q26, Q27, Q28, Q29]), "operationType" : NewBodyOperationType.ADD, "depth" : 5 * mm});
        }
    });
